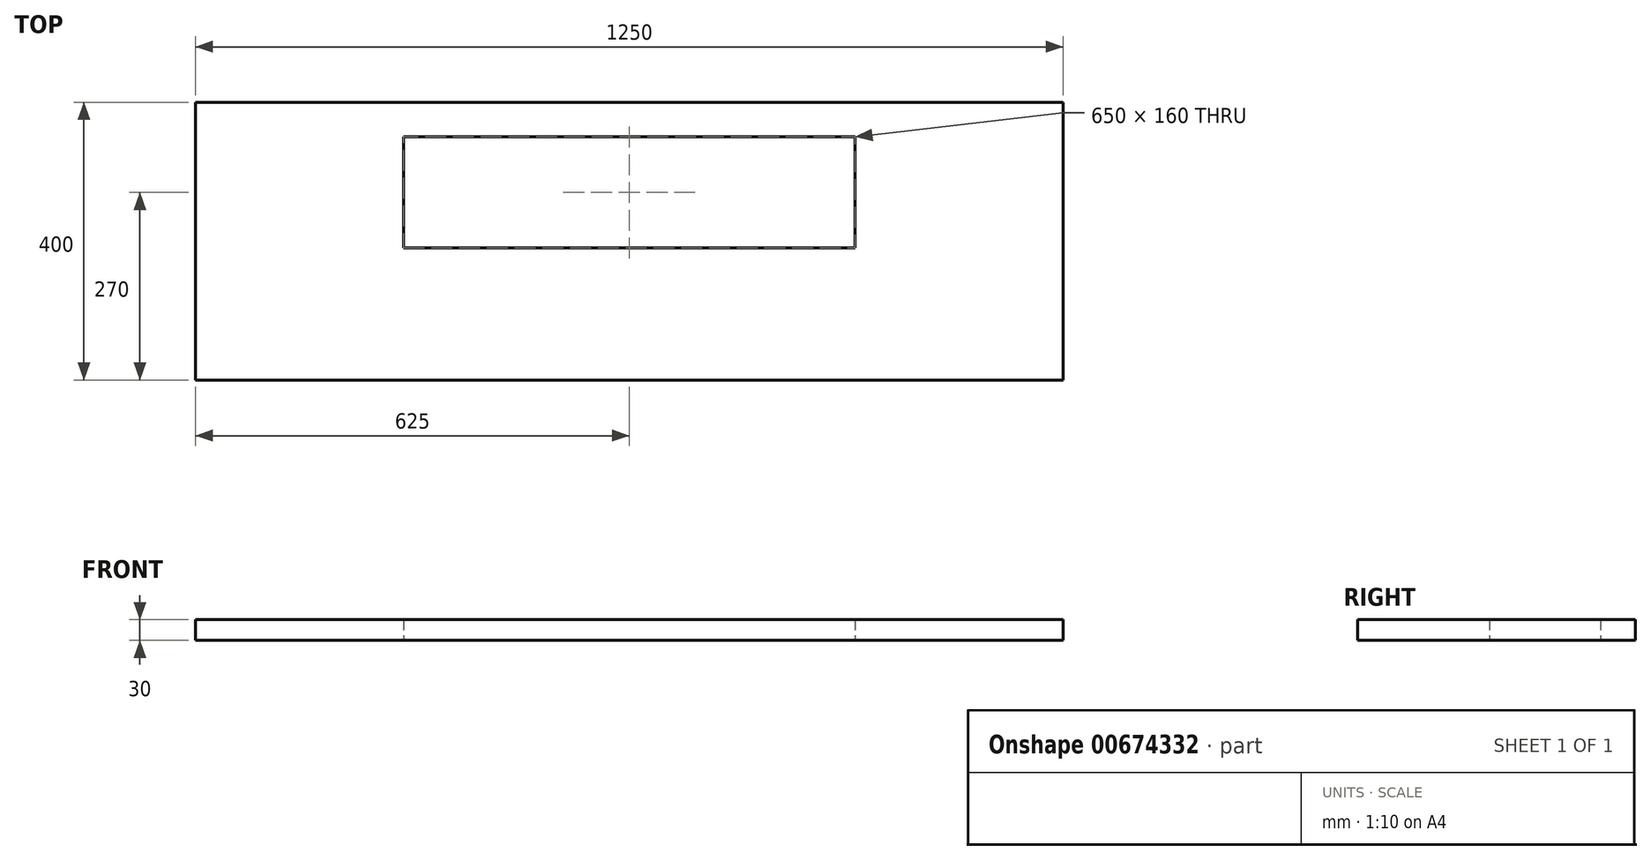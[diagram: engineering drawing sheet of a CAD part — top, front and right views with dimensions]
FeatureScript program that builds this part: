
annotation { "Feature Type Name" : "Feature", "Feature Type Description" : "" }
export const myFeature = defineFeature(function(context is Context, id is Id, definition is map)
    precondition{}
    {
        {
            var Q0;
            Q0=qCreatedBy(makeId("Top.planeOp"),FACE);
            var sketch = newSketch(context, id + "F0", { "sketchPlane" : qUnion([Q0])});
            skLineSegment(sketch, "E0.bottom", {"start": v(325, 80) * mm, "end": v(-325, 80) * mm});
            skLineSegment(sketch, "E0.top", {"start": v(325, -80) * mm, "end": v(-325, -80) * mm});
            skLineSegment(sketch, "E0.left", {"start": v(325, 80) * mm, "end": v(325, -80) * mm});
            skLineSegment(sketch, "E0.right", {"start": v(-325, 80) * mm, "end": v(-325, -80) * mm});
            skPoint(sketch, "E0.middle", {"position": v(0, 0) * mm});
            skLineSegment(sketch, "E1.bottom", {"start": v(-625, 130) * mm, "end": v(625, 130) * mm});
            skLineSegment(sketch, "E1.top", {"start": v(-625, -270) * mm, "end": v(625, -270) * mm});
            skLineSegment(sketch, "E1.left", {"start": v(-625, 130) * mm, "end": v(-625, -270) * mm});
            skLineSegment(sketch, "E1.right", {"start": v(625, 130) * mm, "end": v(625, -270) * mm});
            skPoint(sketch, "E1.middle", {"position": v(0, -70) * mm});
            skSolve(sketch);
        }
        {
            var Q0;
            Q0=makeQuery(id+"F0.imprint","IMPRINT",FACE,{"disambiguationData":[TD([[makeQuery(id+"F0.imprint","IMPRINT",EDGE,{"derivedFrom":sQuery(id+"F0.wireOp",EDGE,"E0.bottom")}),-1.0]])]});
            extrude(context, id + "F1", {"entities" : qUnion([Q0]), "depth" : 30 * mm, "offsetDistance" : 25 * mm});
        }
    });
